# Revit family: DCS_Revit_18_BE1-48RC-N_or_L_and_ASE6-48_Grill_and_Storage_6in_90000785A
name_source: partatom
category: Specialty Equipment
revit_build: Autodesk Revit 2018 (Build: 20170223_1515(x64)
units: mm (PartAtom-declared; Revit-internal decimal feet)

## family parameters
Always vertical = Yes
Cut with Voids When Loaded = Yes
OmniClass Number = 23.40.40.14.17.27
OmniClass Title = Barbecues
Part Type = Normal
Room Calculation Point = No
Round Connector Dimension = Use Diameter
Shared = No
Work Plane-Based = No

## types (2) — shared parameters
Clearance - Below Combustible = 457 mm  [stored 1.49934 ft]
Clearance - Overhead Non-Combustible = 670 mm  [stored 2.19816 ft]
Clearance - Rear Combustible = 457 mm  [stored 1.49934 ft]
Clearance - Rear Non-Combustible = 76 mm  [stored 0.249344 ft]
Clearance - Side Combustible = 457 mm  [stored 1.49934 ft]
Clearance - Side Non-Combustible = 76 mm  [stored 0.249344 ft]
Connector Description - Electrical = 120 V, 15A, GFI electrical outlet
Connector Description - Gas = Operating Pressure NG 4” WC, LPG 11” WC, Connection is 1/2” NPT female
Manufacturer = Fisher & Paykel Appliances
Material - Body = DCS - Stainless Steel
URL = www.dcsappliances.com
Visibility - Clearance Required = Yes

## per-type parameters (varying)
| type | Cavity - Depth | Cavity - Height | Cavity - Width | Description | Model | Product - Depth | Product - Height | Product - Width | Visibility - Clearance Required (Below Countertop) | Visibility - Insulated Jacket |
| Grill and 6" Storage | 578 mm  [stored 1.89633 ft] | 257 mm  [stored 0.843176 ft] | 1314 mm | DCS 48" Series 9 Evolution Grill and 6" Storage Unit | BE1-48RC-N or BE1-48RC-L and ASE6-48 | 695 mm  [stored 2.28018 ft] | 698 mm  [stored 2.29003 ft] | 1369 mm  [stored 4.49147 ft] | Yes | No |
| Grill and 6" Storage with Insulated Jacket | 603 mm | 283 mm  [stored 0.928478 ft] | 1524 mm  [stored 5 ft] | DCS 48" Series 9 Evolution Grill and 6" Storage Unit with 54" Insulated Jacket | BE1-48RC-N or BE1-48RC-L and ASE6-48 with BGA54-IJS | 706 mm | 726 mm  [stored 2.38189 ft] | 1518 mm  [stored 4.98031 ft] | No | Yes |

note: [stored X ft] marks values corroborated as IEEE doubles in the binary element streams (Revit-internal decimal feet)

## geometry (parser evidence)
native form markers: Sweep x26
no freeform markers — native parametric forms only
